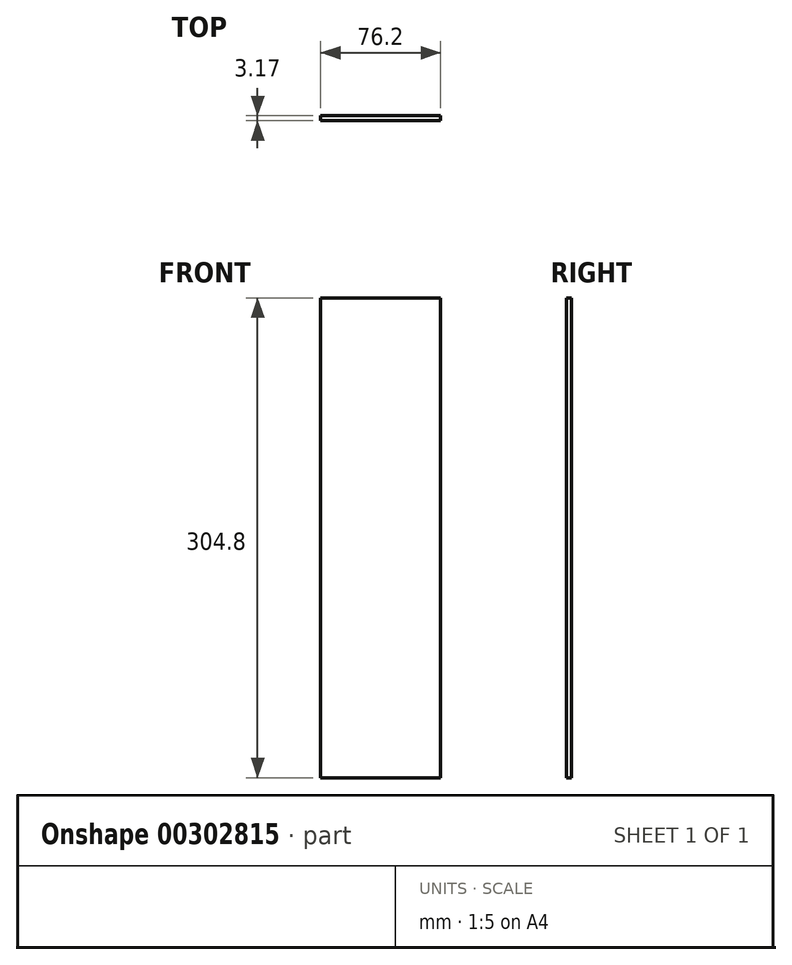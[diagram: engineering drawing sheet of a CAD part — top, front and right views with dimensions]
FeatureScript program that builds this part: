
annotation { "Feature Type Name" : "Feature", "Feature Type Description" : "" }
export const myFeature = defineFeature(function(context is Context, id is Id, definition is map)
    precondition{}
    {
        {
            var Q0;
            Q0=qCreatedBy(makeId("Front.planeOp"),FACE);
            var sketch = newSketch(context, id + "F0", { "sketchPlane" : qUnion([Q0])});
            skLineSegment(sketch, "E0.bottom", {"start": v(-28.31, 258.48) * mm, "end": v(47.89, 258.48) * mm});
            skLineSegment(sketch, "E0.top", {"start": v(-28.31, -46.32) * mm, "end": v(47.89, -46.32) * mm});
            skLineSegment(sketch, "E0.left", {"start": v(-28.31, 258.48) * mm, "end": v(-28.31, -46.32) * mm});
            skLineSegment(sketch, "E0.right", {"start": v(47.89, 258.48) * mm, "end": v(47.89, -46.32) * mm});
            skSolve(sketch);
        }
        {
            var Q0;
            Q0=makeQuery(id+"F0.imprint","IMPRINT",FACE,{"disambiguationData":[TD([[makeQuery(id+"F0.imprint","IMPRINT",EDGE,{"derivedFrom":sQuery(id+"F0.wireOp",EDGE,"E0.bottom")}),-1.0]])]});
            extrude(context, id + "F1", {"entities" : qUnion([Q0]), "depth" : 3.17 * mm});
        }
    });
